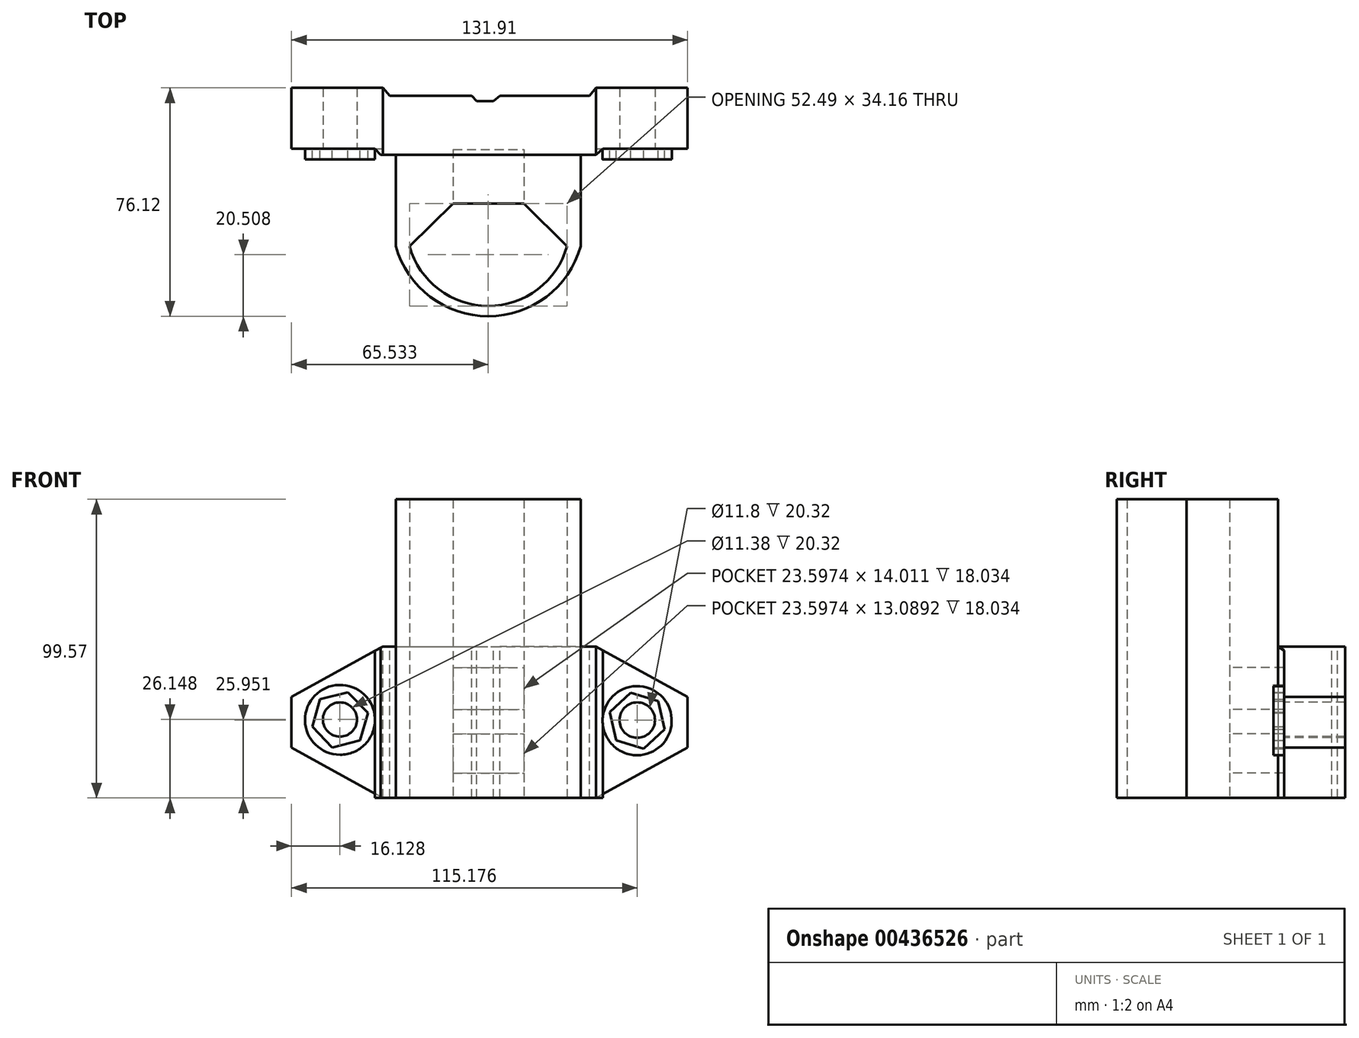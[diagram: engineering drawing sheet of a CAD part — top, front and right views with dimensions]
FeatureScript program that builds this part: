
annotation { "Feature Type Name" : "Feature", "Feature Type Description" : "" }
export const myFeature = defineFeature(function(context is Context, id is Id, definition is map)
    precondition{}
    {
        {
            var Q0;
            Q0=qCreatedBy(makeId("Front.planeOp"),FACE);
            var sketch = newSketch(context, id + "F0", { "sketchPlane" : qUnion([Q0])});
            skLineSegment(sketch, "E0", {"start": v(-70.95, 0) * mm, "end": v(0, 0) * mm});
            skLineSegment(sketch, "E1", {"start": v(0, 0) * mm, "end": v(30.48, -16.74) * mm});
            skLineSegment(sketch, "E2", {"start": v(30.48, -16.74) * mm, "end": v(30.48, -33.73) * mm});
            skLineSegment(sketch, "E3", {"start": v(-70.95, 0) * mm, "end": v(-101.43, -16.74) * mm});
            skLineSegment(sketch, "E4", {"start": v(-101.43, -16.74) * mm, "end": v(-101.43, -33.73) * mm});
            skLineSegment(sketch, "E5", {"start": v(-101.43, -33.73) * mm, "end": v(-70.95, -50.47) * mm});
            skLineSegment(sketch, "E6", {"start": v(-70.95, -50.47) * mm, "end": v(0, -50.47) * mm});
            skLineSegment(sketch, "E7", {"start": v(0, -50.47) * mm, "end": v(30.48, -33.73) * mm});
            skSolve(sketch);
        }
        {
            var Q0;
            Q0 = qSketchRegion(id + "F0", true);
            extrude(context, id + "F1", {"entities" : qUnion([Q0]), "depth" : 20.32 * mm});
        }
        {
            var Q0;
            Q0=makeQuery(id+"F1.opExtrude","SWEPT_FACE",FACE,{"disambiguationData":[OSD([sQuery(id+"F0.wireOp",EDGE,"E6")])]});
            var sketch = newSketch(context, id + "F2", { "sketchPlane" : qUnion([Q0])});
            skLineSegment(sketch, "E8", {"start": v(2.32, 20.28) * mm, "end": v(0, 22.3) * mm});
            skLineSegment(sketch, "E9", {"start": v(0, 22.3) * mm, "end": v(-71.8, 22.3) * mm});
            skLineSegment(sketch, "E10", {"start": v(-71.8, 22.3) * mm, "end": v(-73.64, 20.32) * mm});
            skLineSegment(sketch, "E11", {"start": v(-73.64, 20.32) * mm, "end": v(2.32, 20.28) * mm});
            skSolve(sketch);
        }
        {
            var Q0;
            Q0 = qSketchRegion(id + "F2", true);
            extrude(context, id + "F3", {"entities" : qUnion([Q0]), "operationType" : NewBodyOperationType.ADD, "oppositeDirection" : true, "depth" : 53.85 * mm});
        }
        {
            var Q0;
            {var subQ1=sQuery(id+"F2.wireOp",EDGE,"E11");var subQ5=sQuery(id+"F0.wireOp",EDGE,"E0");Q0=makeQuery(id+"F3.boolean.opBoolean","SPLIT",FACE,{"disambiguationData":[TD([makeQuery(id+"F1.opExtrude","SWEPT_FACE",FACE,{"disambiguationData":[OSD([subQ5])]})])],"derivedFrom":makeQuery(id+"F3.opExtrude","SWEPT_FACE",FACE,{"disambiguationData":[OSD([subQ1])]})});}
            var sketch = newSketch(context, id + "F4", { "sketchPlane" : qUnion([Q0])});
            skLineSegment(sketch, "E12", {"start": v(73.65, -1.47) * mm, "end": v(73.65, 3.38) * mm});
            skLineSegment(sketch, "E13", {"start": v(73.65, 3.38) * mm, "end": v(-2.3, 3.38) * mm});
            skLineSegment(sketch, "E14", {"start": v(-2.3, 3.38) * mm, "end": v(-2.3, -1.27) * mm});
            skLineSegment(sketch, "E15", {"start": v(-2.3, -1.27) * mm, "end": v(0.01, 0) * mm});
            skLineSegment(sketch, "E16", {"start": v(0.01, 0) * mm, "end": v(70.96, 0) * mm});
            skLineSegment(sketch, "E17", {"start": v(70.96, 0) * mm, "end": v(73.65, -1.47) * mm});
            skSolve(sketch);
        }
        {
            var Q0;
            Q0 = qSketchRegion(id + "F4", true);
            extrude(context, id + "F5", {"entities" : qUnion([Q0]), "operationType" : NewBodyOperationType.REMOVE, "oppositeDirection" : true, "depth" : 25.4 * mm});
        }
        {
            var Q0;
            Q0=makeQuery(id+"F5.boolean.opBoolean","MERGE",FACE,{"derivedFrom":[makeQuery(id+"F1.opExtrude","SWEPT_FACE",FACE,{"disambiguationData":[OSD([sQuery(id+"F0.wireOp",EDGE,"E0")])]}),makeQuery(id+"F5.opExtrude","SWEPT_FACE",FACE,{"disambiguationData":[OSD([sQuery(id+"F4.wireOp",EDGE,"E16")])]})]});
            var sketch = newSketch(context, id + "F6", { "sketchPlane" : qUnion([Q0])});
            skLineSegment(sketch, "E18", {"start": v(0, 0) * mm, "end": v(-2.1, -2.58) * mm});
            skLineSegment(sketch, "E19", {"start": v(-2.1, -2.58) * mm, "end": v(-31.97, -2.58) * mm});
            skLineSegment(sketch, "E20", {"start": v(-70.95, 0) * mm, "end": v(-68.66, -2.58) * mm});
            skLineSegment(sketch, "E21", {"start": v(-68.66, -2.58) * mm, "end": v(-41.38, -2.58) * mm});
            skLineSegment(sketch, "E22", {"start": v(-41.38, -2.58) * mm, "end": v(-39.72, -4.42) * mm});
            skLineSegment(sketch, "E23", {"start": v(-39.72, -4.42) * mm, "end": v(-34.19, -4.42) * mm});
            skLineSegment(sketch, "E24", {"start": v(-34.19, -4.42) * mm, "end": v(-31.97, -2.58) * mm});
            skLineSegment(sketch, "E25", {"start": v(-70.95, 0) * mm, "end": v(0, 0) * mm});
            skSolve(sketch);
        }
        {
            var Q0;
            Q0 = qSketchRegion(id + "F6", true);
            extrude(context, id + "F7", {"entities" : qUnion([Q0]), "operationType" : NewBodyOperationType.REMOVE, "oppositeDirection" : true, "depth" : 54.36 * mm});
        }
        {
            var Q0;
            {var subQ0=sQuery(id+"F0.wireOp",EDGE,"E1");var subQ1=sQuery(id+"F0.wireOp",EDGE,"E2");var subQ2=sQuery(id+"F0.wireOp",EDGE,"E7");Q0=makeQuery(id+"F3.boolean.opBoolean","SPLIT",FACE,{"disambiguationData":[TD([makeQuery(id+"F1.opExtrude","SWEPT_FACE",FACE,{"disambiguationData":[OSD([subQ0])]})])],"derivedFrom":makeQuery(id+"F1.opExtrude","CAP_FACE",FACE,{"disambiguationData":[OSD([sQuery(id+"F0.wireOp",EDGE,"E0"),subQ0,subQ1,sQuery(id+"F0.wireOp",EDGE,"E3"),sQuery(id+"F0.wireOp",EDGE,"E4"),sQuery(id+"F0.wireOp",EDGE,"E5"),sQuery(id+"F0.wireOp",EDGE,"E6"),subQ2])],"isStart":false})});}
            var sketch = newSketch(context, id + "F8", { "sketchPlane" : qUnion([Q0])});
            skCircle(sketch, "E26", {"center": v(13.7, -24.73) * mm, "radius": 11.5 * mm});
            skPoint(sketch, "E26.first.point", {"position": v(2.27, -23.41) * mm});
            skPoint(sketch, "E26.second.point", {"position": v(25.18, -25.63) * mm});
            skPoint(sketch, "E26.third.point", {"position": v(19.83, -34.47) * mm});
            skCircle(sketch, "E27", {"center": v(-85.28, -24.44) * mm, "radius": 11.65 * mm});
            skPoint(sketch, "E27.first.point", {"position": v(-73.64, -23.97) * mm});
            skPoint(sketch, "E27.second.point", {"position": v(-96.87, -25.63) * mm});
            skPoint(sketch, "E27.third.point", {"position": v(-82.67, -13.09) * mm});
            skCircle(sketch, "E28.cCircle", {"center": v(-85.28, -24.44) * mm, "radius": 8.28 * mm, "construction": true});
            skLineSegment(sketch, "E28.0", {"start": v(-91.92, -17.56) * mm, "end": v(-82.64, -15.25) * mm});
            skLineSegment(sketch, "E28.1", {"start": v(-82.64, -15.25) * mm, "end": v(-76, -22.13) * mm});
            skLineSegment(sketch, "E28.2", {"start": v(-76, -22.13) * mm, "end": v(-78.64, -31.32) * mm});
            skLineSegment(sketch, "E28.3", {"start": v(-78.64, -31.32) * mm, "end": v(-87.91, -33.64) * mm});
            skLineSegment(sketch, "E28.4", {"start": v(-87.91, -33.64) * mm, "end": v(-94.56, -26.76) * mm});
            skLineSegment(sketch, "E28.5", {"start": v(-94.56, -26.76) * mm, "end": v(-91.92, -17.56) * mm});
            skPoint(sketch, "E28.0.midPoint", {"position": v(-87.28, -16.4) * mm});
            skCircle(sketch, "E29.cCircle", {"center": v(13.7, -24.73) * mm, "radius": 8.32 * mm, "construction": true});
            skLineSegment(sketch, "E29.0", {"start": v(11.55, -15.37) * mm, "end": v(20.74, -18.19) * mm});
            skLineSegment(sketch, "E29.1", {"start": v(20.74, -18.19) * mm, "end": v(22.89, -27.55) * mm});
            skLineSegment(sketch, "E29.2", {"start": v(22.89, -27.55) * mm, "end": v(15.85, -34.1) * mm});
            skLineSegment(sketch, "E29.3", {"start": v(15.85, -34.1) * mm, "end": v(6.67, -31.28) * mm});
            skLineSegment(sketch, "E29.4", {"start": v(6.67, -31.28) * mm, "end": v(4.51, -21.91) * mm});
            skLineSegment(sketch, "E29.5", {"start": v(4.51, -21.91) * mm, "end": v(11.55, -15.37) * mm});
            skPoint(sketch, "E29.0.midPoint", {"position": v(16.14, -16.78) * mm});
            skSolve(sketch);
        }
        {
            var Q0;
            Q0 = qSketchRegion(id + "F8", true);
            extrude(context, id + "F9", {"entities" : qUnion([Q0]), "operationType" : NewBodyOperationType.ADD, "depth" : 3.56 * mm});
        }
        {
            var Q0;
            {var subQ0=sQuery(id+"F0.wireOp",EDGE,"E3");var subQ1=sQuery(id+"F0.wireOp",EDGE,"E5");var subQ2=sQuery(id+"F0.wireOp",EDGE,"E4");Q0=makeQuery(id+"F9.boolean.opBoolean","SPLIT",FACE,{"disambiguationData":[TD([makeQuery(id+"F9.opExtrude","SWEPT_FACE",FACE,{"disambiguationData":[OSD([sQuery(id+"F8.wireOp",EDGE,"E28.0")])]})])],"derivedFrom":makeQuery(id+"F3.boolean.opBoolean","SPLIT",FACE,{"disambiguationData":[TD([makeQuery(id+"F1.opExtrude","SWEPT_FACE",FACE,{"disambiguationData":[OSD([subQ0])]})])],"derivedFrom":makeQuery(id+"F1.opExtrude","CAP_FACE",FACE,{"disambiguationData":[OSD([sQuery(id+"F0.wireOp",EDGE,"E0"),sQuery(id+"F0.wireOp",EDGE,"E1"),sQuery(id+"F0.wireOp",EDGE,"E2"),subQ0,subQ2,subQ1,sQuery(id+"F0.wireOp",EDGE,"E6"),sQuery(id+"F0.wireOp",EDGE,"E7")])],"isStart":false})})});}
            var sketch = newSketch(context, id + "F10", { "sketchPlane" : qUnion([Q0])});
            skCircle(sketch, "E30", {"center": v(-85.3, -24.32) * mm, "radius": 5.69 * mm});
            skCircle(sketch, "E31", {"center": v(13.75, -24.52) * mm, "radius": 5.9 * mm});
            skSolve(sketch);
        }
        {
            var Q0;
            Q0 = qSketchRegion(id + "F10", true);
            extrude(context, id + "F11", {"entities" : qUnion([Q0]), "operationType" : NewBodyOperationType.REMOVE, "oppositeDirection" : true, "depth" : 29.97 * mm});
        }
        {
            var Q0;
            Q0=makeQuery(id+"F3.boolean.opBoolean","MERGE",FACE,{"derivedFrom":[makeQuery(id+"F1.opExtrude","SWEPT_FACE",FACE,{"disambiguationData":[OSD([sQuery(id+"F0.wireOp",EDGE,"E6")])]}),makeQuery(id+"F3.opExtrude","CAP_FACE",FACE,{"disambiguationData":[OSD([sQuery(id+"F2.wireOp",EDGE,"E8"),sQuery(id+"F2.wireOp",EDGE,"E9"),sQuery(id+"F2.wireOp",EDGE,"E10"),sQuery(id+"F2.wireOp",EDGE,"E11")])],"isStart":true})]});
            var sketch = newSketch(context, id + "F12", { "sketchPlane" : qUnion([Q0])});
            skLineSegment(sketch, "E32", {"start": v(-66.71, 22.3) * mm, "end": v(-66.71, 52.79) * mm});
            skLineSegment(sketch, "E33", {"start": v(-5.08, 22.3) * mm, "end": v(-5.08, 52.79) * mm});
            skLineSegment(sketch, "E34", {"start": v(-66.71, 52.79) * mm, "end": v(-62.14, 52.79) * mm});
            skLineSegment(sketch, "E35", {"start": v(-62.14, 52.79) * mm, "end": v(-47.58, 38.53) * mm});
            skLineSegment(sketch, "E36", {"start": v(-5.08, 52.79) * mm, "end": v(-9.65, 52.79) * mm});
            skLineSegment(sketch, "E37", {"start": v(-9.65, 52.79) * mm, "end": v(-23.98, 38.53) * mm});
            skLineSegment(sketch, "E38", {"start": v(-47.58, 38.53) * mm, "end": v(-23.98, 38.53) * mm});
            skLineSegment(sketch, "E39", {"start": v(-66.71, 22.3) * mm, "end": v(-5.08, 22.3) * mm});
            skSolve(sketch);
        }
        {
            var Q0;
            Q0 = qSketchRegion(id + "F12", true);
            extrude(context, id + "F13", {"entities" : qUnion([Q0]), "operationType" : NewBodyOperationType.ADD, "oppositeDirection" : true, "depth" : 99.57 * mm});
        }
        {
            var Q0;
            Q0=makeQuery(id+"F13.opExtrude","SWEPT_FACE",FACE,{"disambiguationData":[OSD([sQuery(id+"F12.wireOp",EDGE,"E38")])]});
            var sketch = newSketch(context, id + "F14", { "sketchPlane" : qUnion([Q0])});
            skLineSegment(sketch, "E40.bottom", {"start": v(-47.58, -42.22) * mm, "end": v(-23.98, -42.22) * mm});
            skLineSegment(sketch, "E40.top", {"start": v(-47.58, -29.13) * mm, "end": v(-23.98, -29.13) * mm});
            skLineSegment(sketch, "E40.left", {"start": v(-47.58, -42.22) * mm, "end": v(-47.58, -29.13) * mm});
            skLineSegment(sketch, "E40.right", {"start": v(-23.98, -42.22) * mm, "end": v(-23.98, -29.13) * mm});
            skLineSegment(sketch, "E41.bottom", {"start": v(-47.58, -7) * mm, "end": v(-23.98, -7) * mm});
            skLineSegment(sketch, "E41.top", {"start": v(-47.58, -21.02) * mm, "end": v(-23.98, -21.02) * mm});
            skLineSegment(sketch, "E41.left", {"start": v(-47.58, -7) * mm, "end": v(-47.58, -21.02) * mm});
            skLineSegment(sketch, "E41.right", {"start": v(-23.98, -7) * mm, "end": v(-23.98, -21.02) * mm});
            skSolve(sketch);
        }
        {
            var Q0;
            Q0 = qSketchRegion(id + "F14", true);
            extrude(context, id + "F15", {"entities" : qUnion([Q0]), "operationType" : NewBodyOperationType.REMOVE, "oppositeDirection" : true, "depth" : 18.03 * mm});
        }
        {
            var Q0;
            Q0=makeQuery(id+"F13.boolean.opBoolean","MERGE",FACE,{"derivedFrom":[makeQuery(id+"F3.boolean.opBoolean","MERGE",FACE,{"derivedFrom":[makeQuery(id+"F1.opExtrude","SWEPT_FACE",FACE,{"disambiguationData":[OSD([sQuery(id+"F0.wireOp",EDGE,"E6")])]}),makeQuery(id+"F3.opExtrude","CAP_FACE",FACE,{"disambiguationData":[OSD([sQuery(id+"F2.wireOp",EDGE,"E8"),sQuery(id+"F2.wireOp",EDGE,"E9"),sQuery(id+"F2.wireOp",EDGE,"E10"),sQuery(id+"F2.wireOp",EDGE,"E11")])],"isStart":true})]}),makeQuery(id+"F13.opExtrude","CAP_FACE",FACE,{"disambiguationData":[OSD([sQuery(id+"F12.wireOp",EDGE,"E32"),sQuery(id+"F12.wireOp",EDGE,"E33"),sQuery(id+"F12.wireOp",EDGE,"E34"),sQuery(id+"F12.wireOp",EDGE,"E35"),sQuery(id+"F12.wireOp",EDGE,"E36"),sQuery(id+"F12.wireOp",EDGE,"E37"),sQuery(id+"F12.wireOp",EDGE,"E38"),sQuery(id+"F12.wireOp",EDGE,"E39")])],"isStart":true})]});
            var sketch = newSketch(context, id + "F16", { "sketchPlane" : qUnion([Q0])});
            skArc(sketch, "E42", {"start": v(-5.08, 52.79) * mm, "mid": v(-35.9, 76.12) * mm, "end": v(-66.71, 52.79) * mm});
            skArc(sketch, "E43", {"start": v(-9.65, 52.79) * mm, "mid": v(-35.9, 72.7) * mm, "end": v(-62.14, 52.79) * mm});
            skLineSegment(sketch, "E44", {"start": v(-66.71, 52.79) * mm, "end": v(-62.14, 52.79) * mm});
            skLineSegment(sketch, "E45", {"start": v(-9.65, 52.79) * mm, "end": v(-5.08, 52.79) * mm});
            skSolve(sketch);
        }
        {
            var Q0;
            Q0 = qSketchRegion(id + "F16", true);
            extrude(context, id + "F17", {"entities" : qUnion([Q0]), "operationType" : NewBodyOperationType.ADD, "oppositeDirection" : true, "depth" : 99.57 * mm});
        }
    });
